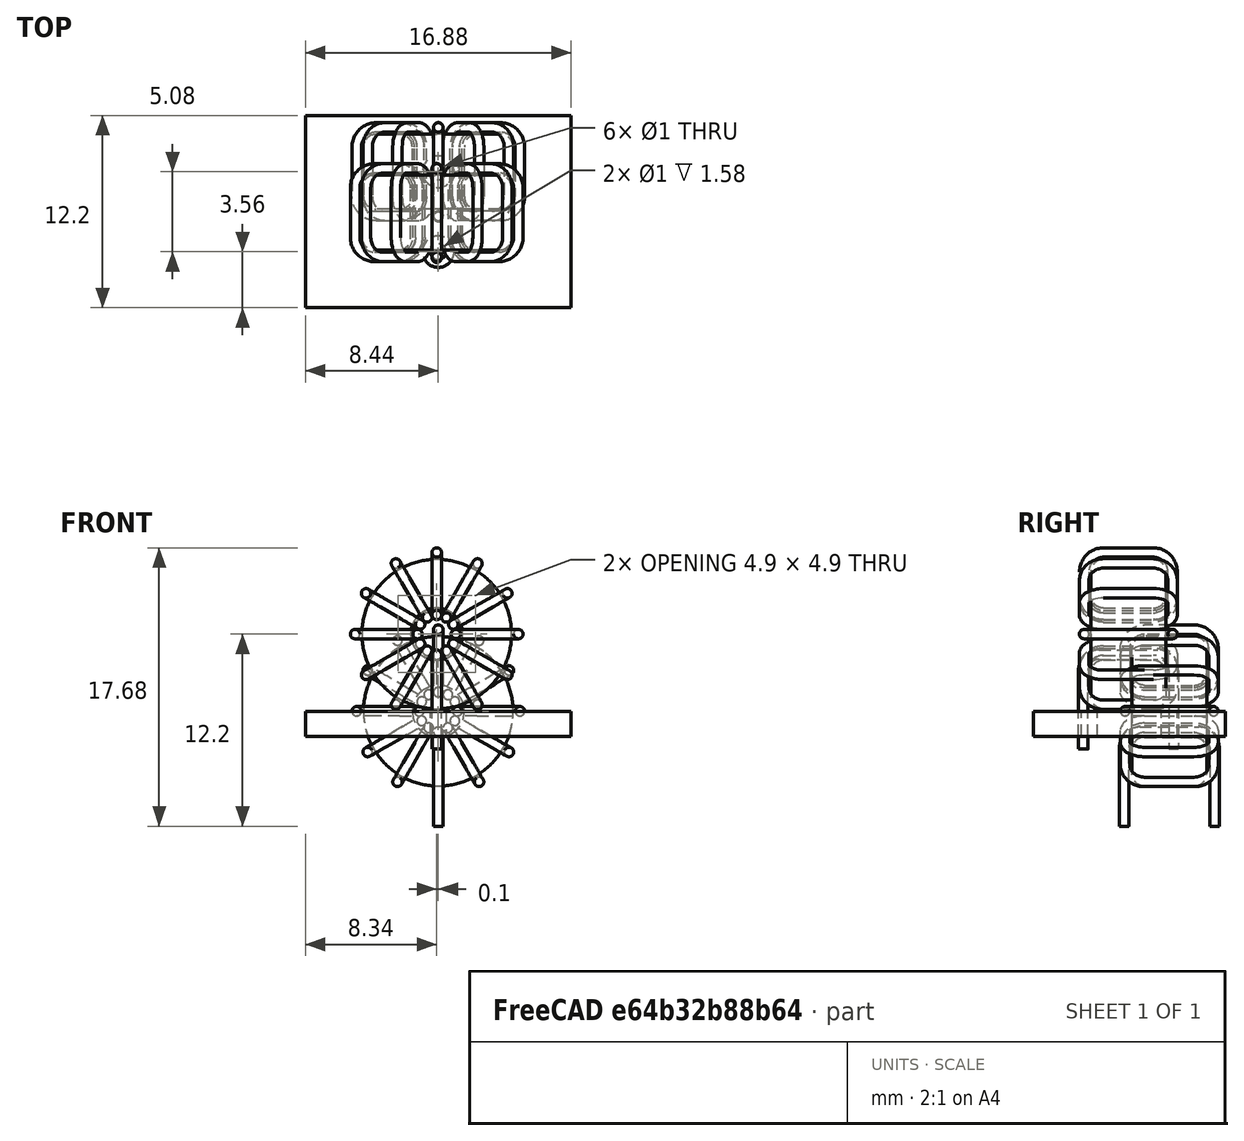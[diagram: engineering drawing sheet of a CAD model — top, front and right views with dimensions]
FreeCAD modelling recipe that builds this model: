
FCSTD DOCUMENT  (FreeCAD 0.19R24415 (Git))
Label: simple_toroid
License: All rights reserved
LicenseURL: http://en.wikipedia.org/wiki/All_rights_reserved
objects: PartDesign::Body×11, PartDesign::FeatureBase×10, Sketcher::SketchObject×5, Part::FeaturePython×5, Part::Feature×3, Part::Sweep×2, PartDesign::Revolution×1, PartDesign::PolarPattern×1, Part::Compound×1, App::DocumentObjectGroup×1
note: 40 computed .brp shape members not serialized (recipe doc carries the construction recipe); baked Part::Feature solids carry a one-line shape summary decoded from their .brp

FEATURE [Sketcher::SketchObject] Sketch
  FullyConstrained = true
  MapMode = 5
  Support = -> [XY_Plane]
  sketch-geometry (11):
    g0: LineSegment StartX=2.45 StartY=2.375 StartZ=0 EndX=3.95 EndY=2.375 EndZ=0
    g1: LineSegment StartX=4.75 StartY=1.575 StartZ=0 EndX=4.75 EndY=-1.575 EndZ=0
    g2: LineSegment StartX=3.95 StartY=-2.375 StartZ=0 EndX=2.45 EndY=-2.375 EndZ=0
    g3: LineSegment StartX=1.65 StartY=-1.575 StartZ=0 EndX=1.65 EndY=1.575 EndZ=0
    g4: ArcOfCircle CenterX=2.45 CenterY=1.575 CenterZ=0 NormalX=0 NormalY=0 NormalZ=1 AngleXU=0 Radius=0.8 StartAngle=1.5708 EndAngle=3.14159
    g5: ArcOfCircle CenterX=3.95 CenterY=1.575 CenterZ=0 NormalX=0 NormalY=0 NormalZ=1 AngleXU=0 Radius=0.8 StartAngle=0 EndAngle=1.5708
    g6: ArcOfCircle CenterX=3.95 CenterY=-1.575 CenterZ=0 NormalX=0 NormalY=0 NormalZ=1 AngleXU=0 Radius=0.8 StartAngle=4.71239 EndAngle=6.28319
    g7: ArcOfCircle CenterX=2.45 CenterY=-1.575 CenterZ=0 NormalX=0 NormalY=0 NormalZ=1 AngleXU=0 Radius=0.8 StartAngle=3.14159 EndAngle=4.71239
    g8: LineSegment StartX=1.65 StartY=1.575 StartZ=0 EndX=0 EndY=0 EndZ=0
    g9: LineSegment StartX=0 StartY=0 StartZ=0 EndX=1.65 EndY=-1.575 EndZ=0
    g10: LineSegment StartX=1.65 StartY=-1.575 StartZ=0 EndX=0 EndY=-1.575 EndZ=0
  constraints (27):
    c: Horizontal(g0)
    c: Horizontal(g2)
    c: Vertical(g1)
    c: Vertical(g3)
    c: Tangent(g0,g4) = 1.5708
    c: Tangent(g3,g4) = 1.5708
    c: Tangent(g0,g5) = 1.5708
    c: Tangent(g1,g5) = 1.5708
    c: Tangent(g1,g6) = 1.5708
    c: Tangent(g2,g6) = 1.5708
    c: Tangent(g2,g7) = 1.5708
    c: Tangent(g3,g7) = 1.5708
    c: Equal(g6,g7)
    c: Equal(g7,g4)
    c: Equal(g4,g5)
    c: Coincident(g3,g8)
    c: Coincident(g8,g-1)
    c: Coincident(g8,g9)
    c: Coincident(g9,g3)
    c: Equal(g8,g9)
    c: Radius(g4) = 0.8
    c: DistanceY(g2,g0) = 4.75
    c: Coincident(g10,g3)
    c: PointOnObject(g10,g-2)
    c: Horizontal(g10)
    c: Distance(g10) = 1.65
    c: DistanceX(g10,g1) = 4.75
FEATURE [PartDesign::Revolution] Revolution
  Angle = 360
  Axis = (0,1,0)
  Base = (0,0,0)
  Profile = -> Sketch
  ReferenceAxis = -> Sketch [V_Axis]
  Reversed = true
FEATURE [Sketcher::SketchObject] Sketch001  label="wire_path"
  ExternalGeometry = -> [Revolution]
  FullyConstrained = false
  MapMode = 5
  Placement = pos=(0,0,0) rot=(0.57735,0.57735,0.57735;2.0944rad)
  Support = -> [YZ_Plane]
  sketch-geometry (9):
    g0: LineSegment StartX=-2.875 StartY=-7.3 StartZ=0 EndX=-2.875 EndY=-2.3 EndZ=0
    g1: LineSegment StartX=-1.875 StartY=-1.3 StartZ=0 EndX=1.875 EndY=-1.3 EndZ=0
    g2: LineSegment StartX=2.875 StartY=-2.3 StartZ=0 EndX=2.875 EndY=-7.3 EndZ=0
    g3: ArcOfCircle CenterX=1.875 CenterY=-2.3 CenterZ=0 NormalX=0 NormalY=0 NormalZ=1 AngleXU=0 Radius=1 StartAngle=0 EndAngle=1.5708
    g4: ArcOfCircle CenterX=-1.875 CenterY=-2.3 CenterZ=0 NormalX=0 NormalY=0 NormalZ=1 AngleXU=0 Radius=1 StartAngle=1.5708 EndAngle=3.14159
    g5: LineSegment StartX=-1.875 StartY=-1.3 StartZ=0 EndX=0 EndY=0 EndZ=0
    g6: LineSegment StartX=0 StartY=0 StartZ=0 EndX=1.875 EndY=-1.3 EndZ=0
    g7: LineSegment StartX=-2.875 StartY=-3.0823 StartZ=0 EndX=-2.375 EndY=-3.0823 EndZ=0
    g8: LineSegment StartX=0 StartY=-1.3 StartZ=0 EndX=0 EndY=0 EndZ=0
  constraints (24):
    c: Vertical(g0)
    c: Horizontal(g1)
    c: Vertical(g2)
    c: Tangent(g1,g3) = 1.5708
    c: Tangent(g2,g3) = 1.5708
    c: Tangent(g0,g4) = 1.5708
    c: Tangent(g1,g4) = 1.5708
    c: Equal(g0,g2)
    c: Coincident(g1,g5)
    c: Coincident(g5,g-1)
    c: Coincident(g5,g6)
    c: Coincident(g6,g1)
    c: Equal(g6,g5)
    c: Distance(g2) = 5
    c: Equal(g3,g4)
    c: Radius(g3) = 1
    c: PointOnObject(g7,g0)
    c: PointOnObject(g7,g-3)
    c: Horizontal(g7)
    c: PointOnObject(g8,g1)
    c: Coincident(g8,g-1)
    c: Vertical(g8)
    c: Distance(g8) = 1.3
    c: Distance(g7) = 0.5
FEATURE [Sketcher::SketchObject] Sketch002  label="wire_profile"
  FullyConstrained = false
  MapMode = 5
  Placement = pos=(0,0,0) rot=(1,0,0;1.5708rad)
  Support = -> [XZ_Plane]
  sketch-geometry (1):
    g0: Circle CenterX=0 CenterY=-1.3079 CenterZ=0 NormalX=0 NormalY=0 NormalZ=1 AngleXU=0 Radius=0.3
  constraints (2):
    c: PointOnObject(g0,g-2)
    c: Diameter(g0) = 0.6
FEATURE [Sketcher::SketchObject] Sketch003
  FullyConstrained = true
  MapMode = 5
  Support = -> [XY_Plane]
  expr: Constraints[53] = Sketch.Constraints[26]
  expr: Constraints[52] = Sketch.Constraints[25]
  expr: Constraints[47] = Sketch.Constraints[20]
  expr: Constraints[26] = Sketch.Constraints[26]
  expr: Constraints[25] = Sketch.Constraints[25]
  expr: Constraints[21] = Sketch.Constraints[21]
  expr: Constraints[48] = Sketch.Constraints[21]
  expr: Constraints[20] = Sketch.Constraints[20]
  sketch-geometry (22):
    g0: LineSegment StartX=2.45 StartY=2.375 StartZ=0 EndX=3.95 EndY=2.375 EndZ=0
    g1: LineSegment StartX=4.75 StartY=1.575 StartZ=0 EndX=4.75 EndY=-1.575 EndZ=0
    g2: LineSegment StartX=3.95 StartY=-2.375 StartZ=0 EndX=2.45 EndY=-2.375 EndZ=0
    g3: LineSegment StartX=1.65 StartY=-1.575 StartZ=0 EndX=1.65 EndY=1.575 EndZ=0
    g4: ArcOfCircle CenterX=2.45 CenterY=1.575 CenterZ=0 NormalX=0 NormalY=0 NormalZ=1 AngleXU=0 Radius=0.8 StartAngle=1.5708 EndAngle=3.14159
    g5: ArcOfCircle CenterX=3.95 CenterY=1.575 CenterZ=0 NormalX=0 NormalY=0 NormalZ=1 AngleXU=0 Radius=0.8 StartAngle=0 EndAngle=1.5708
    g6: ArcOfCircle CenterX=3.95 CenterY=-1.575 CenterZ=0 NormalX=0 NormalY=0 NormalZ=1 AngleXU=0 Radius=0.8 StartAngle=4.71239 EndAngle=6.28319
    g7: ArcOfCircle CenterX=2.45 CenterY=-1.575 CenterZ=0 NormalX=0 NormalY=0 NormalZ=1 AngleXU=0 Radius=0.8 StartAngle=3.14159 EndAngle=4.71239
    g8: LineSegment StartX=1.65 StartY=1.575 StartZ=0 EndX=0 EndY=0 EndZ=0
    g9: LineSegment StartX=0 StartY=0 StartZ=0 EndX=1.65 EndY=-1.575 EndZ=0
    g10: LineSegment StartX=1.65 StartY=-1.575 StartZ=0 EndX=0 EndY=-1.575 EndZ=0
    g11: LineSegment StartX=2.45 StartY=2.375 StartZ=0 EndX=3.95 EndY=2.375 EndZ=0
    g12: LineSegment StartX=4.75 StartY=1.575 StartZ=0 EndX=4.75 EndY=-1.575 EndZ=0
    g13: LineSegment StartX=3.95 StartY=-2.375 StartZ=0 EndX=2.45 EndY=-2.375 EndZ=0
    g14: LineSegment StartX=1.65 StartY=-1.575 StartZ=0 EndX=1.65 EndY=1.575 EndZ=0
    g15: ArcOfCircle CenterX=2.45 CenterY=1.575 CenterZ=0 NormalX=0 NormalY=0 NormalZ=1 AngleXU=0 Radius=0.8 StartAngle=1.5708 EndAngle=3.14159
    g16: ArcOfCircle CenterX=3.95 CenterY=1.575 CenterZ=0 NormalX=0 NormalY=0 NormalZ=1 AngleXU=0 Radius=0.8 StartAngle=0 EndAngle=1.5708
    g17: ArcOfCircle CenterX=3.95 CenterY=-1.575 CenterZ=0 NormalX=0 NormalY=0 NormalZ=1 AngleXU=0 Radius=0.8 StartAngle=4.71239 EndAngle=6.28319
    g18: ArcOfCircle CenterX=2.45 CenterY=-1.575 CenterZ=0 NormalX=0 NormalY=0 NormalZ=1 AngleXU=0 Radius=0.8 StartAngle=3.14159 EndAngle=4.71239
    g19: LineSegment StartX=1.65 StartY=1.575 StartZ=0 EndX=0 EndY=0 EndZ=0
    g20: LineSegment StartX=0 StartY=0 StartZ=0 EndX=1.65 EndY=-1.575 EndZ=0
    g21: LineSegment StartX=1.65 StartY=-1.575 StartZ=0 EndX=0 EndY=-1.575 EndZ=0
  constraints (54):
    c: Horizontal(g0)
    c: Horizontal(g2)
    c: Vertical(g1)
    c: Vertical(g3)
    c: Tangent(g0,g4) = 1.5708
    c: Tangent(g3,g4) = 1.5708
    c: Tangent(g0,g5) = 1.5708
    c: Tangent(g1,g5) = 1.5708
    c: Tangent(g1,g6) = 1.5708
    c: Tangent(g2,g6) = 1.5708
    c: Tangent(g2,g7) = 1.5708
    c: Tangent(g3,g7) = 1.5708
    c: Equal(g6,g7)
    c: Equal(g7,g4)
    c: Equal(g4,g5)
    c: Coincident(g3,g8)
    c: Coincident(g8,g-1)
    c: Coincident(g8,g9)
    c: Coincident(g9,g3)
    c: Equal(g8,g9)
    c: Radius(g4) = 0.8
    c: DistanceY(g2,g0) = 4.75
    c: Coincident(g10,g3)
    c: PointOnObject(g10,g-2)
    c: Horizontal(g10)
    c: Distance(g10) = 1.65
    c: DistanceX(g10,g1) = 4.75
    c: Horizontal(g11)
    c: Horizontal(g13)
    c: Vertical(g12)
    c: Vertical(g14)
    c: Tangent(g11,g15) = 1.5708
    c: Tangent(g14,g15) = 1.5708
    c: Tangent(g11,g16) = 1.5708
    c: Tangent(g12,g16) = 1.5708
    c: Tangent(g12,g17) = 1.5708
    c: Tangent(g13,g17) = 1.5708
    c: Tangent(g13,g18) = 1.5708
    c: Tangent(g14,g18) = 1.5708
    c: Equal(g17,g18)
    c: Equal(g18,g15)
    c: Equal(g15,g16)
    c: Coincident(g14,g19)
    c: Coincident(g19,g-1)
    c: Coincident(g19,g20)
    c: Coincident(g20,g14)
    c: Equal(g19,g20)
    c: Radius(g15) = 0.8
    c: DistanceY(g13,g11) = 4.75
    c: Coincident(g21,g14)
    c: PointOnObject(g21,g-2)
    c: Horizontal(g21)
    c: Distance(g21) = 1.65
    c: DistanceX(g21,g12) = 4.75
FEATURE [Sketcher::SketchObject] Sketch004
  FullyConstrained = false
  MapMode = 5
  Placement = pos=(0,0,0) rot=(1,0,0;1.5708rad)
  Support = -> [XZ_Plane]
  sketch-geometry (1):
    g0: Circle CenterX=1.21595 CenterY=0 CenterZ=0 NormalX=0 NormalY=0 NormalZ=1 AngleXU=0 Radius=0.3
  constraints (2):
    c: PointOnObject(g0,g-1)
    c: Diameter(g0) = 0.6
FEATURE [PartDesign::PolarPattern] PolarPattern
  Angle = 360
  Axis = -> Y_Axis
  BaseFeature = -> Revolution
  Occurrences = 6
  Originals = -> [Revolution]
FEATURE [PartDesign::Body] Body
  Group = -> [Sketch,Revolution,Sketch001,Sketch002,Sketch003,Sketch004,PolarPattern]
  Origin = -> Origin
  Tip = -> PolarPattern
FEATURE [Part::Sweep] Sweep
  Frenet = false
  Sections = -> [Sketch002]
  Solid = true
  Spine = -> Sketch001
  Transition = 1
FEATURE [Part::Sweep] Sweep001
  Frenet = false
  Sections = -> [Sketch004]
  Solid = true
  Spine = -> Sketch003
  Transition = 1
FEATURE [PartDesign::FeatureBase] Clone
  BaseFeature = -> Sweep001
FEATURE [PartDesign::Body] Body001
  Group = -> [Clone]
  Origin = -> Origin001
  Placement = pos=(0,0,0) rot=(0,1,0;5.75959rad)
  Tip = -> Clone
FEATURE [PartDesign::FeatureBase] Clone001
  BaseFeature = -> Sweep001
FEATURE [PartDesign::Body] Body002
  Group = -> [Clone001]
  Origin = -> Origin002
  Placement = pos=(0,0,0) rot=(0,1,0;5.23599rad)
  Tip = -> Clone001
FEATURE [PartDesign::FeatureBase] Clone002
  BaseFeature = -> Sweep001
FEATURE [PartDesign::Body] Body003
  Group = -> [Clone002]
  Origin = -> Origin003
  Placement = pos=(0,0,0) rot=(0,1,0;4.71239rad)
  Tip = -> Clone002
FEATURE [PartDesign::FeatureBase] Clone003
  BaseFeature = -> Sweep001
FEATURE [PartDesign::Body] Body004
  Group = -> [Clone003]
  Origin = -> Origin004
  Placement = pos=(0,0,0) rot=(0,1,0;4.18879rad)
  Tip = -> Clone003
FEATURE [PartDesign::FeatureBase] Clone004
  BaseFeature = -> Sweep001
FEATURE [PartDesign::Body] Body005
  Group = -> [Clone004]
  Origin = -> Origin005
  Placement = pos=(0,0,0) rot=(0,1,0;3.66519rad)
  Tip = -> Clone004
FEATURE [PartDesign::FeatureBase] Clone005
  BaseFeature = -> Sweep001
FEATURE [PartDesign::Body] Body006
  Group = -> [Clone005]
  Origin = -> Origin006
  Placement = pos=(0,0,0) rot=(0,1,0;3.14159rad)
  Tip = -> Clone005
FEATURE [PartDesign::FeatureBase] Clone006
  BaseFeature = -> Sweep001
FEATURE [PartDesign::Body] Body007
  Group = -> [Clone006]
  Origin = -> Origin007
  Placement = pos=(0,0,0) rot=(0,1,0;2.61799rad)
  Tip = -> Clone006
FEATURE [PartDesign::FeatureBase] Clone007
  BaseFeature = -> Sweep001
FEATURE [PartDesign::Body] Body008
  Group = -> [Clone007]
  Origin = -> Origin008
  Placement = pos=(0,0,0) rot=(0,1,0;2.0944rad)
  Tip = -> Clone007
FEATURE [PartDesign::FeatureBase] Clone008
  BaseFeature = -> Sweep001
FEATURE [PartDesign::Body] Body009
  Group = -> [Clone008]
  Origin = -> Origin009
  Placement = pos=(0,0,0) rot=(0,1,0;0.523599rad)
  Tip = -> Clone008
FEATURE [PartDesign::FeatureBase] Clone009
  BaseFeature = -> Sweep001
FEATURE [PartDesign::Body] Body010
  Group = -> [Clone009]
  Origin = -> Origin010
  Placement = pos=(0,0,0) rot=(0,1,0;1.0472rad)
  Tip = -> Clone009
FEATURE [Part::Compound] Compound
  Links = -> [Sweep,Sweep001,Body001,Body002,Body003,Body004,Body005,Body006,Body007,Body008,Body009,Body010]
FEATURE [Part::FeaturePython] FCrtYd_lines  label="FCrtYd"  # a2plus imported part (geometry in sourceFile) (typed FeaturePython)
  fixedPosition = true
FEATURE [Part::FeaturePython] FFab_lines  label="FFab"  # a2plus imported part (geometry in sourceFile) (typed FeaturePython)
  fixedPosition = true
FEATURE [Part::FeaturePython] FSilk_lines  label="FrontSilk"  # a2plus imported part (geometry in sourceFile) (typed FeaturePython)
  fixedPosition = true
FEATURE [Part::FeaturePython] THPs  label="PTHs"  # a2plus imported part (geometry in sourceFile) (typed FeaturePython)
  fixedPosition = true
FEATURE [Part::Feature] Shape001003  label="TopPads"
  shape: bbox 2 x 7.08 x 0.01 mm, 8 faces, 2 solids (baked)
FEATURE [Part::Feature] Shape001004  label="BotPads"
  shape: bbox 2 x 7.08 x 0.01 mm, 8 faces, 2 solids (baked)
FEATURE [Part::FeaturePython] newPCB  label="Pcb"  # a2plus imported part (geometry in sourceFile) (typed FeaturePython)
  fixedPosition = true
FEATURE [App::DocumentObjectGroup] L_Toroid_Vertical_L10_0mm_W5_0mm_P5_08mm_fp
  Group = -> [FCrtYd_lines,FFab_lines,FSilk_lines,Shape001003,Shape001004,THPs,newPCB]
FEATURE [Part::Feature] Shape  label="vertical_toroid_9.5x4.75x3.3"
  shape: bbox 11.22 x 6.547 x 12.91 mm, 221 faces, 13 solids (baked)
